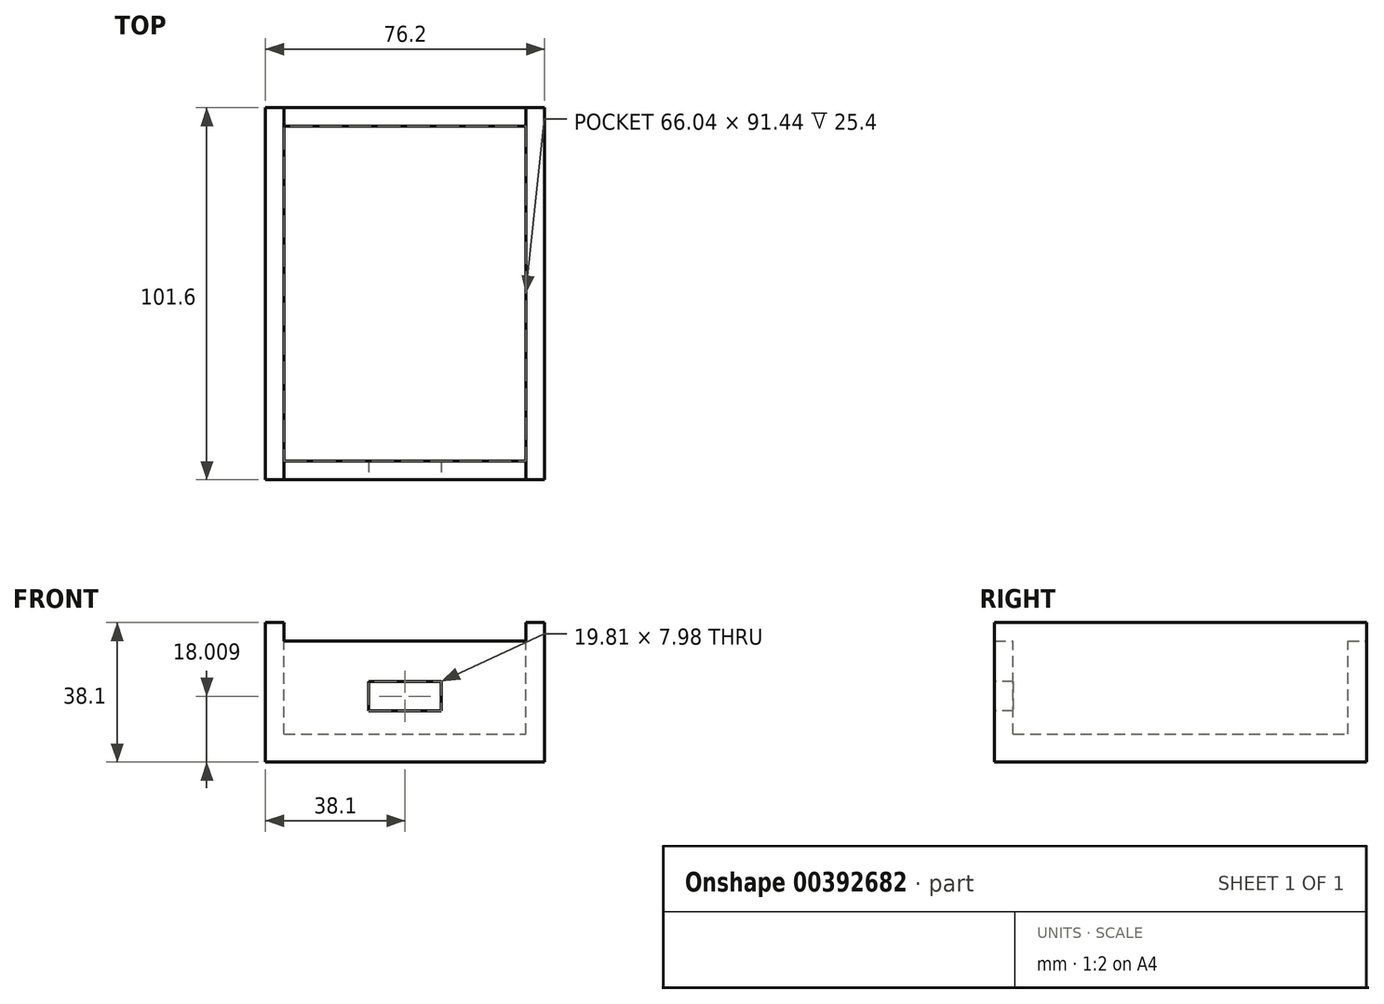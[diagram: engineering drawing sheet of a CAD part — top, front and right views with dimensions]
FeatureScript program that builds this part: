
annotation { "Feature Type Name" : "Feature", "Feature Type Description" : "" }
export const myFeature = defineFeature(function(context is Context, id is Id, definition is map)
    precondition{}
    {
        {
            var Q0;
            Q0=qCreatedBy(makeId("Front.planeOp"),FACE);
            var sketch = newSketch(context, id + "F0", { "sketchPlane" : qUnion([Q0])});
            skLineSegment(sketch, "E0", {"start": v(0, 0) * mm, "end": v(-38.1, 0) * mm});
            skLineSegment(sketch, "E1", {"start": v(0, 0) * mm, "end": v(38.1, 0) * mm});
            skLineSegment(sketch, "E2", {"start": v(-38.1, 0) * mm, "end": v(-38.1, 38.1) * mm});
            skLineSegment(sketch, "E3", {"start": v(38.1, 0) * mm, "end": v(38.1, 38.1) * mm});
            skLineSegment(sketch, "E4", {"start": v(-38.1, 38.1) * mm, "end": v(-33.02, 38.1) * mm});
            skLineSegment(sketch, "E5", {"start": v(-38.1, 0) * mm, "end": v(-33.02, 0) * mm});
            skLineSegment(sketch, "E6", {"start": v(-33.02, 0) * mm, "end": v(-33.02, 5.08) * mm});
            skLineSegment(sketch, "E7", {"start": v(-33.02, 5.08) * mm, "end": v(33.02, 5.08) * mm});
            skLineSegment(sketch, "E8", {"start": v(33.02, 5.08) * mm, "end": v(33.02, 0) * mm});
            skLineSegment(sketch, "E9", {"start": v(33.02, 0) * mm, "end": v(38.1, 0) * mm});
            skLineSegment(sketch, "E10", {"start": v(38.1, 38.1) * mm, "end": v(33.02, 38.1) * mm});
            skLineSegment(sketch, "E11", {"start": v(-33.02, 38.1) * mm, "end": v(-33.02, 5.08) * mm});
            skLineSegment(sketch, "E12", {"start": v(33.02, 38.1) * mm, "end": v(33.02, 5.08) * mm});
            skLineSegment(sketch, "E13", {"start": v(-33.02, 38.1) * mm, "end": v(-33.02, 33.02) * mm});
            skLineSegment(sketch, "E14", {"start": v(33.02, 38.1) * mm, "end": v(33.02, 33.02) * mm});
            skLineSegment(sketch, "E15", {"start": v(33.02, 33.02) * mm, "end": v(-33.02, 33.02) * mm});
            skSolve(sketch);
        }
        {
            var Q0;
            Q0=makeQuery(id+"F0.imprint","IMPRINT",FACE,{"disambiguationData":[TD([[makeQuery(id+"F0.imprint","IMPRINT",EDGE,{"derivedFrom":sQuery(id+"F0.wireOp",EDGE,"E2")}),-1.0]])]});
            var Q1;
            Q1=makeQuery(id+"F0.imprint","IMPRINT",FACE,{"disambiguationData":[TD([[makeQuery(id+"F0.imprint","IMPRINT",EDGE,{"derivedFrom":sQuery(id+"F0.wireOp",EDGE,"E0")}),-1.0]])]});
            var Q2;
            Q2=makeQuery(id+"F0.imprint","IMPRINT",FACE,{"disambiguationData":[TD([[makeQuery(id+"F0.imprint","IMPRINT",EDGE,{"derivedFrom":sQuery(id+"F0.wireOp",EDGE,"E3")}),1.0]])]});
            var Q3;
            Q3=makeQuery(id+"F0.imprint","IMPRINT",FACE,{"disambiguationData":[TD([[makeQuery(id+"F0.imprint","IMPRINT",EDGE,{"derivedFrom":sQuery(id+"F0.wireOp",EDGE,"E7")}),1.0]])]});
            extrude(context, id + "F1", {"entities" : qUnion([Q0, Q1, Q2, Q3]), "depth" : 101.6 * mm});
        }
        {
            var Q0;
            Q0=makeQuery(id+"F1.opExtrude","SWEPT_FACE",FACE,{"disambiguationData":[OSD([sQuery(id+"F0.wireOp",EDGE,"E15")])]});
            var sketch = newSketch(context, id + "F2", { "sketchPlane" : qUnion([Q0])});
            skPoint(sketch, "E16.middle", {"position": v(0, -50.8) * mm});
            skLineSegment(sketch, "E17.bottom", {"start": v(-33.02, -5.08) * mm, "end": v(33.02, -5.08) * mm});
            skLineSegment(sketch, "E17.top", {"start": v(-33.02, -96.52) * mm, "end": v(33.02, -96.52) * mm});
            skLineSegment(sketch, "E17.left", {"start": v(-33.02, -5.08) * mm, "end": v(-33.02, -96.52) * mm});
            skLineSegment(sketch, "E17.right", {"start": v(33.02, -5.08) * mm, "end": v(33.02, -96.52) * mm});
            skSolve(sketch);
        }
        {
            var Q0;
            Q0 = qSketchRegion(id + "F2", true);
            extrude(context, id + "F3", {"entities" : qUnion([Q0]), "operationType" : NewBodyOperationType.REMOVE, "oppositeDirection" : true, "depth" : 25.4 * mm});
        }
        {
            var Q0;
            Q0=makeQuery(id+"F1.opExtrude","CAP_FACE",FACE,{"disambiguationData":[OSD([sQuery(id+"F0.wireOp",EDGE,"E0"),sQuery(id+"F0.wireOp",EDGE,"E1"),sQuery(id+"F0.wireOp",EDGE,"E2"),sQuery(id+"F0.wireOp",EDGE,"E3"),sQuery(id+"F0.wireOp",EDGE,"E4"),sQuery(id+"F0.wireOp",EDGE,"E5"),sQuery(id+"F0.wireOp",EDGE,"E9"),sQuery(id+"F0.wireOp",EDGE,"E10"),sQuery(id+"F0.wireOp",EDGE,"E13"),sQuery(id+"F0.wireOp",EDGE,"E14"),sQuery(id+"F0.wireOp",EDGE,"E15")])],"isStart":false});
            var sketch = newSketch(context, id + "F4", { "sketchPlane" : qUnion([Q0])});
            skLineSegment(sketch, "E18.bottom", {"start": v(-9.9, 22) * mm, "end": v(9.9, 22) * mm});
            skLineSegment(sketch, "E18.top", {"start": v(-9.9, 14.02) * mm, "end": v(9.9, 14.02) * mm});
            skLineSegment(sketch, "E18.left", {"start": v(-9.9, 22) * mm, "end": v(-9.9, 14.02) * mm});
            skLineSegment(sketch, "E18.right", {"start": v(9.9, 22) * mm, "end": v(9.9, 14.02) * mm});
            skPoint(sketch, "E18.middle", {"position": v(0, 18) * mm});
            skSolve(sketch);
        }
        {
            var Q0;
            Q0 = qSketchRegion(id + "F4", true);
            extrude(context, id + "F5", {"entities" : qUnion([Q0]), "operationType" : NewBodyOperationType.REMOVE, "oppositeDirection" : true, "depth" : 12.7 * mm});
        }
    });
